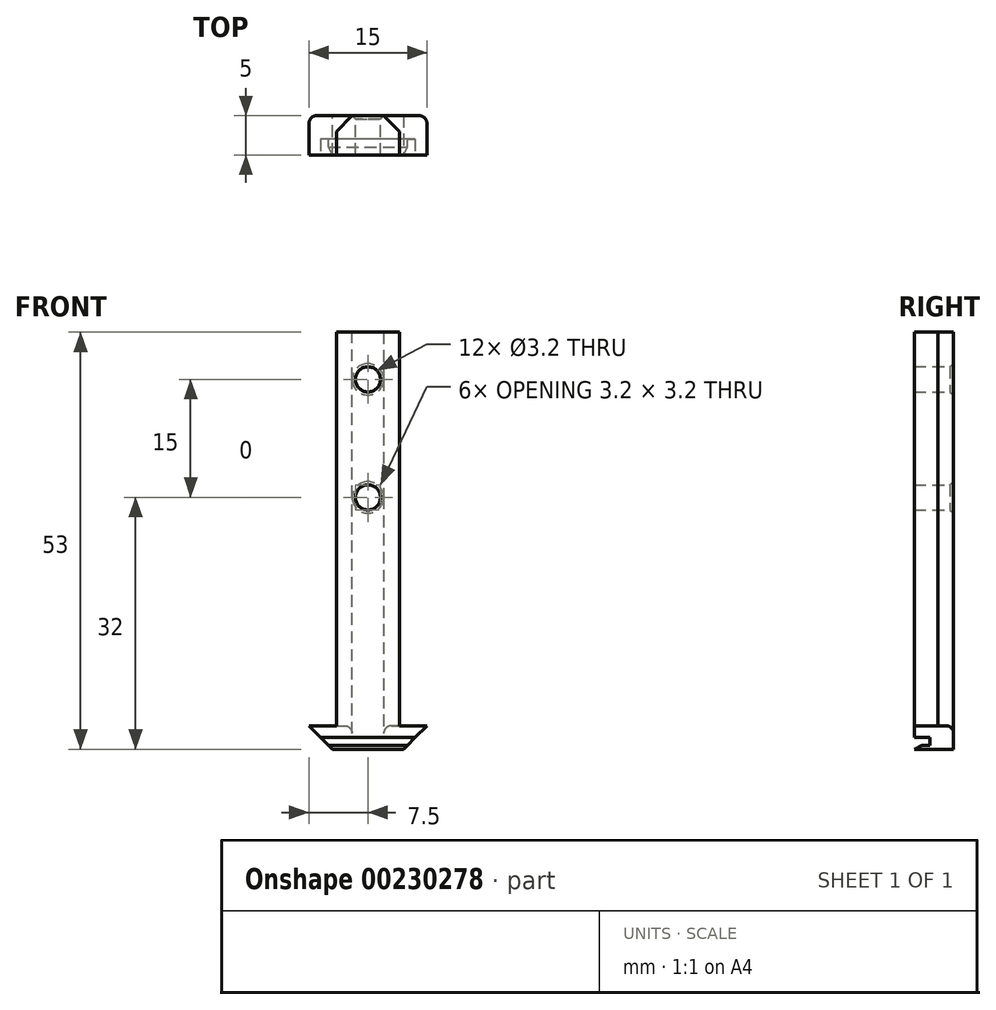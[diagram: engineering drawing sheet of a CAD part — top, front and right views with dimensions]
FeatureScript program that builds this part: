
annotation { "Feature Type Name" : "Feature", "Feature Type Description" : "" }
export const myFeature = defineFeature(function(context is Context, id is Id, definition is map)
    precondition{}
    {
        {
            var Q0;
            Q0=qCreatedBy(makeId("Front.planeOp"),FACE);
            var sketch = newSketch(context, id + "F0", { "sketchPlane" : qUnion([Q0])});
            skLineSegment(sketch, "E0.bottom", {"start": v(4, -25) * mm, "end": v(-4, -25) * mm});
            skLineSegment(sketch, "E0.top", {"start": v(4, 25) * mm, "end": v(-4, 25) * mm});
            skLineSegment(sketch, "E0.left", {"start": v(4, -25) * mm, "end": v(4, 25) * mm});
            skLineSegment(sketch, "E0.right", {"start": v(-4, -25) * mm, "end": v(-4, 25) * mm});
            skPoint(sketch, "E0.middle", {"position": v(0, 0) * mm});
            skLineSegment(sketch, "E1.bottom", {"start": v(-7.5, -25) * mm, "end": v(7.5, -25) * mm});
            skLineSegment(sketch, "E1.top", {"start": v(-7.5, -28) * mm, "end": v(7.5, -28) * mm});
            skLineSegment(sketch, "E1.left", {"start": v(-7.5, -25) * mm, "end": v(-7.5, -28) * mm});
            skLineSegment(sketch, "E1.right", {"start": v(7.5, -25) * mm, "end": v(7.5, -28) * mm});
            skSolve(sketch);
        }
        {
            var Q0;
            Q0=makeQuery(id+"F0.imprint","IMPRINT",FACE,{"disambiguationData":[TD([[makeQuery(id+"F0.imprint","IMPRINT",EDGE,{"derivedFrom":sQuery(id+"F0.wireOp",EDGE,"E0.top")}),1.0]])]});
            var Q1;
            Q1=makeQuery(id+"F0.imprint","IMPRINT",FACE,{"disambiguationData":[TD([[makeQuery(id+"F0.imprint","IMPRINT",EDGE,{"derivedFrom":sQuery(id+"F0.wireOp",EDGE,"E1.top")}),1.0]])]});
            extrude(context, id + "F1", {"entities" : qUnion([Q0, Q1]), "endBound" : BoundingType.SYMMETRIC, "depth" : 5 * mm});
        }
        {
            var Q0;
            Q0=makeQuery(id+"F1.opExtrude","CAP_FACE",FACE,{"disambiguationData":[OSD([sQuery(id+"F0.wireOp",EDGE,"E0.top"),sQuery(id+"F0.wireOp",EDGE,"E0.left"),sQuery(id+"F0.wireOp",EDGE,"E0.right"),sQuery(id+"F0.wireOp",EDGE,"E1.bottom"),sQuery(id+"F0.wireOp",EDGE,"E1.top"),sQuery(id+"F0.wireOp",EDGE,"E1.left"),sQuery(id+"F0.wireOp",EDGE,"E1.right")])],"isStart":false});
            var sketch = newSketch(context, id + "F2", { "sketchPlane" : qUnion([Q0])});
            skLineSegment(sketch, "E2.bottom", {"start": v(8, -27.5) * mm, "end": v(-8, -27.5) * mm});
            skLineSegment(sketch, "E2.top", {"start": v(8, -26.5) * mm, "end": v(-8, -26.5) * mm});
            skLineSegment(sketch, "E2.left", {"start": v(8, -27.5) * mm, "end": v(8, -26.5) * mm});
            skLineSegment(sketch, "E2.right", {"start": v(-8, -27.5) * mm, "end": v(-8, -26.5) * mm});
            skPoint(sketch, "E2.middle", {"position": v(0, -27) * mm});
            skSolve(sketch);
        }
        {
            var Q0;
            {var subQ0=sQuery(id+"F2.wireOp",EDGE,"E2.bottom");var subQ1=makeQuery(id+"F1.opExtrude","CAP_EDGE",EDGE,{"disambiguationData":[OSD([sQuery(id+"F0.wireOp",EDGE,"E1.right")])],"isStart":false});var subQ2=makeQuery(id+"F2.imprint","INTERSECT",VERTEX,{"derivedFrom":[subQ1,subQ0]});Q0=makeQuery(id+"F2.imprint","IMPRINT",FACE,{"disambiguationData":[TD([[makeQuery(id+"F2.imprint","IMPRINT",EDGE,{"disambiguationData":[TD([[subQ2,-1.0]])],"derivedFrom":subQ0}),-1.0]])]});}
            var Q1;
            {var subQ0=sQuery(id+"F2.wireOp",EDGE,"E2.right");Q1=makeQuery(id+"F2.imprint","IMPRINT",FACE,{"disambiguationData":[TD([[makeQuery(id+"F2.imprint","IMPRINT",EDGE,{"derivedFrom":subQ0}),-1.0]])]});}
            var Q2;
            {var subQ0=sQuery(id+"F2.wireOp",EDGE,"E2.left");Q2=makeQuery(id+"F2.imprint","IMPRINT",FACE,{"disambiguationData":[TD([[makeQuery(id+"F2.imprint","IMPRINT",EDGE,{"derivedFrom":subQ0}),1.0]])]});}
            extrude(context, id + "F3", {"entities" : qUnion([Q0, Q1, Q2]), "operationType" : NewBodyOperationType.REMOVE, "oppositeDirection" : true, "depth" : 2 * mm});
        }
        {
            var Q0;
            Q0=makeQuery(id+"F1.opExtrude","SWEPT_EDGE",EDGE,{"disambiguationData":[OSD([sQuery(id+"F0.wireOp",EDGE,"E1.top"),sQuery(id+"F0.wireOp",EDGE,"E1.left")])]});
            var Q1;
            Q1=makeQuery(id+"F1.opExtrude","SWEPT_EDGE",EDGE,{"disambiguationData":[OSD([sQuery(id+"F0.wireOp",EDGE,"E1.top"),sQuery(id+"F0.wireOp",EDGE,"E1.right")])]});
            chamfer(context, id + "F4", {"entities" : qUnion([Q0, Q1]), "width" : 3 * mm, "tangentPropagation" : true});
        }
        {
            var Q0;
            Q0=makeQuery(id+"F1.opExtrude","CAP_EDGE",EDGE,{"disambiguationData":[OSD([sQuery(id+"F0.wireOp",EDGE,"E0.right")])],"isStart":true});
            var Q1;
            Q1=makeQuery(id+"F1.opExtrude","CAP_EDGE",EDGE,{"disambiguationData":[OSD([sQuery(id+"F0.wireOp",EDGE,"E0.left")])],"isStart":true});
            chamfer(context, id + "F5", {"entities" : qUnion([Q0, Q1]), "width" : 2 * mm, "tangentPropagation" : true});
        }
        {
            var Q0;
            Q0=makeQuery(id+"F3.boolean.opBoolean","COPY",EDGE,{"derivedFrom":makeQuery(id+"F3.opExtrude","CAP_EDGE",EDGE,{"disambiguationData":[OSD([sQuery(id+"F2.wireOp",EDGE,"E2.bottom")])],"isStart":true})});
            chamfer(context, id + "F6", {"entities" : qUnion([Q0]), "chamferType" : ChamferType.TWO_OFFSETS, "width1" : 0.5 * mm, "oppositeDirection" : false, "width2" : 1 * mm, "tangentPropagation" : true});
        }
        {
            var Q0;
            {var subQ0=sQuery(id+"F0.wireOp",EDGE,"E1.bottom");Q0=makeQuery(id+"F1.opExtrude","CAP_EDGE",EDGE,{"disambiguationData":[OSD([subQ0]),TDD([makeQuery(id+"F0.imprint","IMPRINT",EDGE,{"disambiguationData":[TD([[makeQuery(id+"F0.imprint","INTERSECT",VERTEX,{"derivedFrom":[sQuery(id+"F0.wireOp",EDGE,"E0.right"),subQ0]}),1.0]])],"derivedFrom":subQ0})])],"isStart":true});}
            var Q1;
            {var subQ0=sQuery(id+"F0.wireOp",EDGE,"E1.bottom");Q1=makeQuery(id+"F1.opExtrude","CAP_EDGE",EDGE,{"disambiguationData":[OSD([subQ0]),TDD([makeQuery(id+"F0.imprint","IMPRINT",EDGE,{"disambiguationData":[TD([[makeQuery(id+"F0.imprint","INTERSECT",VERTEX,{"derivedFrom":[sQuery(id+"F0.wireOp",EDGE,"E0.left"),subQ0]}),-1.0]])],"derivedFrom":subQ0})])],"isStart":true});}
            fillet(context, id + "F7", {"entities" : qUnion([Q0, Q1]), "radius" : 1 * mm, "tangentPropagation" : true, "allowEdgeOverflow" : false});
        }
        {
            var Q0;
            Q0=makeQuery(id+"F1.opExtrude","CAP_FACE",FACE,{"disambiguationData":[OSD([sQuery(id+"F0.wireOp",EDGE,"E0.top"),sQuery(id+"F0.wireOp",EDGE,"E0.left"),sQuery(id+"F0.wireOp",EDGE,"E0.right"),sQuery(id+"F0.wireOp",EDGE,"E1.bottom"),sQuery(id+"F0.wireOp",EDGE,"E1.top"),sQuery(id+"F0.wireOp",EDGE,"E1.left"),sQuery(id+"F0.wireOp",EDGE,"E1.right")])],"isStart":true});
            var sketch = newSketch(context, id + "F8", { "sketchPlane" : qUnion([Q0])});
            skPoint(sketch, "E3", {"position": v(0, 19) * mm});
            skPoint(sketch, "E4", {"position": v(0, 4) * mm});
            skSolve(sketch);
        }
        {
            var Q0;
            Q0=sQuery(id+"F8.wireOp",VERTEX,"E3");
            var Q1;
            Q1=sQuery(id+"F8.wireOp",VERTEX,"E4");
            var Q2;
            Q2=makeQuery(id+"F1.opExtrude","SWEPT_BODY",BODY,{"disambiguationData":[OSD([sQuery(id+"F0.wireOp",EDGE,"E0.top"),sQuery(id+"F0.wireOp",EDGE,"E0.left"),sQuery(id+"F0.wireOp",EDGE,"E0.right"),sQuery(id+"F0.wireOp",EDGE,"E1.bottom"),sQuery(id+"F0.wireOp",EDGE,"E1.top"),sQuery(id+"F0.wireOp",EDGE,"E1.left"),sQuery(id+"F0.wireOp",EDGE,"E1.right")])]});
            hole(context, id + "F9", {"style" : HoleStyle.C_SINK, "endStyle" : HoleEndStyle.THROUGH, "holeDiameter" : 3.2 * mm, "cSinkDiameter" : 4 * mm, "cSinkAngle" : 82 * degree, "locations" : qUnion([Q0, Q1]), "scope" : qUnion([Q2]), "isTappedThrough" : true});
        }
    });
